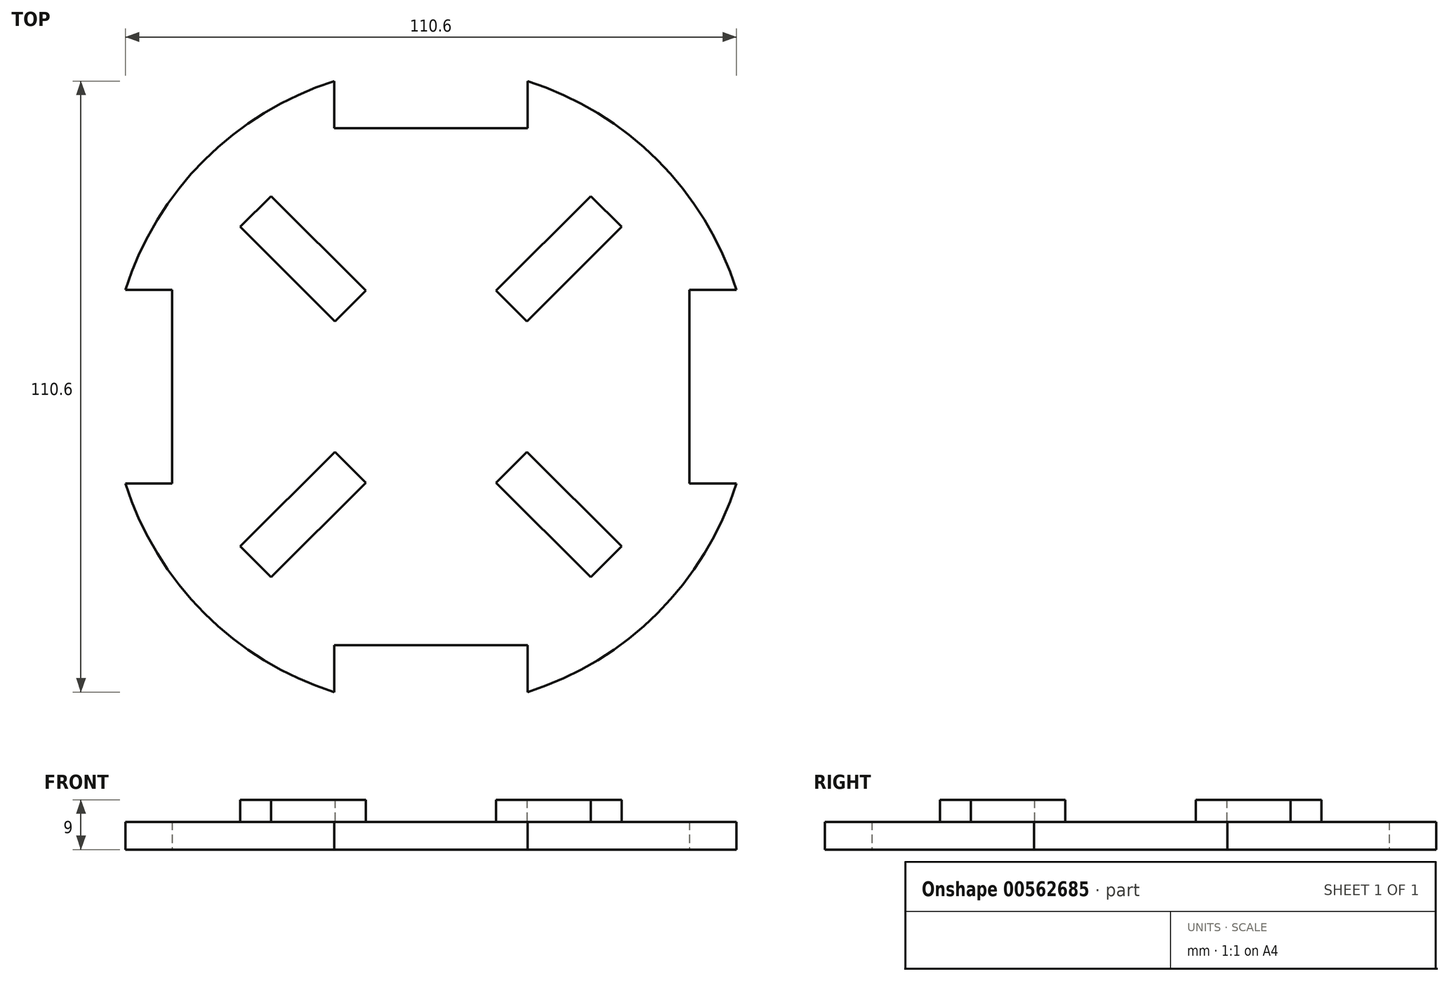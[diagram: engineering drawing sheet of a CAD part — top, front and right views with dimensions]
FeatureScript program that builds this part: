
annotation { "Feature Type Name" : "Feature", "Feature Type Description" : "" }
export const myFeature = defineFeature(function(context is Context, id is Id, definition is map)
    precondition{}
    {
        {
            var Q0;
            Q0=qCreatedBy(makeId("Top.planeOp"),FACE);
            var sketch = newSketch(context, id + "F0", { "sketchPlane" : qUnion([Q0])});
            skCircle(sketch, "E0", {"center": v(0, 0) * mm, "radius": 58 * mm});
            skLineSegment(sketch, "E1.bottom", {"start": v(-17.5, 55.3) * mm, "end": v(17.5, 55.3) * mm});
            skLineSegment(sketch, "E1.top", {"start": v(-17.5, 46.8) * mm, "end": v(17.5, 46.8) * mm});
            skLineSegment(sketch, "E1.left", {"start": v(-17.5, 55.3) * mm, "end": v(-17.5, 46.8) * mm});
            skLineSegment(sketch, "E1.right", {"start": v(17.5, 55.3) * mm, "end": v(17.5, 46.8) * mm});
            skLineSegment(sketch, "E2.1.0", {"start": v(-46.8, -17.5) * mm, "end": v(-46.8, 17.5) * mm});
            skLineSegment(sketch, "E2.1.1", {"start": v(-55.3, -17.5) * mm, "end": v(-46.8, -17.5) * mm});
            skLineSegment(sketch, "E2.1.2", {"start": v(-55.3, -17.5) * mm, "end": v(-55.3, 17.5) * mm});
            skLineSegment(sketch, "E2.1.3", {"start": v(-55.3, 17.5) * mm, "end": v(-46.8, 17.5) * mm});
            skLineSegment(sketch, "E2.2.0", {"start": v(17.5, -46.8) * mm, "end": v(-17.5, -46.8) * mm});
            skLineSegment(sketch, "E2.2.1", {"start": v(17.5, -55.3) * mm, "end": v(17.5, -46.8) * mm});
            skLineSegment(sketch, "E2.2.2", {"start": v(17.5, -55.3) * mm, "end": v(-17.5, -55.3) * mm});
            skLineSegment(sketch, "E2.2.3", {"start": v(-17.5, -55.3) * mm, "end": v(-17.5, -46.8) * mm});
            skLineSegment(sketch, "E3.1.3.0", {"start": v(46.8, 17.5) * mm, "end": v(46.8, -17.5) * mm});
            skLineSegment(sketch, "E3.3.3.0", {"start": v(55.3, 17.5) * mm, "end": v(46.8, 17.5) * mm});
            skLineSegment(sketch, "E3.6.3.0", {"start": v(55.3, 17.5) * mm, "end": v(55.3, -17.5) * mm});
            skLineSegment(sketch, "E3.9.3.0", {"start": v(55.3, -17.5) * mm, "end": v(46.8, -17.5) * mm});
            skSolve(sketch);
        }
        {
            var Q0;
            Q0=makeQuery(id+"F0.imprint","IMPRINT",FACE,{"disambiguationData":[TD([[makeQuery(id+"F0.imprint","IMPRINT",EDGE,{"derivedFrom":sQuery(id+"F0.wireOp",EDGE,"E1.top")}),-1.0]])]});
            extrude(context, id + "F1", {"entities" : qUnion([Q0]), "depth" : 5 * mm, "offsetDistance" : 25 * mm});
        }
        {
            var Q0;
            Q0=makeQuery(id+"F1.opExtrude","CAP_FACE",FACE,{"disambiguationData":[OSD([sQuery(id+"F0.wireOp",EDGE,"E0"),sQuery(id+"F0.wireOp",EDGE,"E1.top"),sQuery(id+"F0.wireOp",EDGE,"E1.left"),sQuery(id+"F0.wireOp",EDGE,"E1.right"),sQuery(id+"F0.wireOp",EDGE,"E2.1.0"),sQuery(id+"F0.wireOp",EDGE,"E2.1.1"),sQuery(id+"F0.wireOp",EDGE,"E2.1.3"),sQuery(id+"F0.wireOp",EDGE,"E2.2.0"),sQuery(id+"F0.wireOp",EDGE,"E2.2.1"),sQuery(id+"F0.wireOp",EDGE,"E2.2.3"),sQuery(id+"F0.wireOp",EDGE,"E3.1.3.0"),sQuery(id+"F0.wireOp",EDGE,"E3.3.3.0"),sQuery(id+"F0.wireOp",EDGE,"E3.9.3.0")])],"isStart":false});
            var sketch = newSketch(context, id + "F2", { "sketchPlane" : qUnion([Q0])});
            skLineSegment(sketch, "E4", {"start": v(-41.01, 41.01) * mm, "end": v(41.01, -41.01) * mm, "construction": true});
            skLineSegment(sketch, "E5", {"start": v(-34.5, 28.92) * mm, "end": v(-28.92, 34.5) * mm});
            skLineSegment(sketch, "E6", {"start": v(-28.92, 34.5) * mm, "end": v(-11.8, 17.38) * mm});
            skLineSegment(sketch, "E7", {"start": v(-11.8, 17.38) * mm, "end": v(-17.38, 11.8) * mm});
            skLineSegment(sketch, "E8", {"start": v(-17.38, 11.8) * mm, "end": v(-34.5, 28.92) * mm});
            skPoint(sketch, "E9", {"position": v(-31.71, 31.71) * mm});
            skPoint(sketch, "E10", {"position": v(-14.58, 14.58) * mm});
            skLineSegment(sketch, "E11.1.0", {"start": v(-34.5, -28.92) * mm, "end": v(-17.38, -11.8) * mm});
            skLineSegment(sketch, "E11.1.1", {"start": v(-11.8, -17.38) * mm, "end": v(-28.92, -34.5) * mm});
            skLineSegment(sketch, "E11.1.2", {"start": v(-28.92, -34.5) * mm, "end": v(-34.5, -28.92) * mm});
            skLineSegment(sketch, "E11.1.3", {"start": v(-17.38, -11.8) * mm, "end": v(-11.8, -17.38) * mm});
            skLineSegment(sketch, "E11.2.0", {"start": v(28.92, -34.5) * mm, "end": v(11.8, -17.38) * mm});
            skLineSegment(sketch, "E11.2.1", {"start": v(17.38, -11.8) * mm, "end": v(34.5, -28.92) * mm});
            skLineSegment(sketch, "E11.2.2", {"start": v(34.5, -28.92) * mm, "end": v(28.92, -34.5) * mm});
            skLineSegment(sketch, "E11.2.3", {"start": v(11.8, -17.38) * mm, "end": v(17.38, -11.8) * mm});
            skLineSegment(sketch, "E11.3.0", {"start": v(34.5, 28.92) * mm, "end": v(17.38, 11.8) * mm});
            skLineSegment(sketch, "E11.3.1", {"start": v(11.8, 17.38) * mm, "end": v(28.92, 34.5) * mm});
            skLineSegment(sketch, "E11.3.2", {"start": v(28.92, 34.5) * mm, "end": v(34.5, 28.92) * mm});
            skLineSegment(sketch, "E11.3.3", {"start": v(17.38, 11.8) * mm, "end": v(11.8, 17.38) * mm});
            skPoint(sketch, "E11.center", {"position": v(0, 0) * mm});
            skSolve(sketch);
        }
        {
            var Q0;
            Q0=makeQuery(id+"F2.imprint","IMPRINT",FACE,{"disambiguationData":[TD([[makeQuery(id+"F2.imprint","IMPRINT",EDGE,{"derivedFrom":sQuery(id+"F2.wireOp",EDGE,"E5")}),-1.0]])]});
            var Q1;
            Q1=makeQuery(id+"F2.imprint","IMPRINT",FACE,{"disambiguationData":[TD([[makeQuery(id+"F2.imprint","IMPRINT",EDGE,{"derivedFrom":sQuery(id+"F2.wireOp",EDGE,"E11.3.0")}),-1.0]])]});
            var Q2;
            Q2=makeQuery(id+"F2.imprint","IMPRINT",FACE,{"disambiguationData":[TD([[makeQuery(id+"F2.imprint","IMPRINT",EDGE,{"derivedFrom":sQuery(id+"F2.wireOp",EDGE,"E11.2.0")}),-1.0]])]});
            var Q3;
            Q3=makeQuery(id+"F2.imprint","IMPRINT",FACE,{"disambiguationData":[TD([[makeQuery(id+"F2.imprint","IMPRINT",EDGE,{"derivedFrom":sQuery(id+"F2.wireOp",EDGE,"E11.1.0")}),-1.0]])]});
            extrude(context, id + "F3", {"entities" : qUnion([Q0, Q1, Q2, Q3]), "operationType" : NewBodyOperationType.ADD, "depth" : 4 * mm, "offsetDistance" : 25 * mm});
        }
    });
